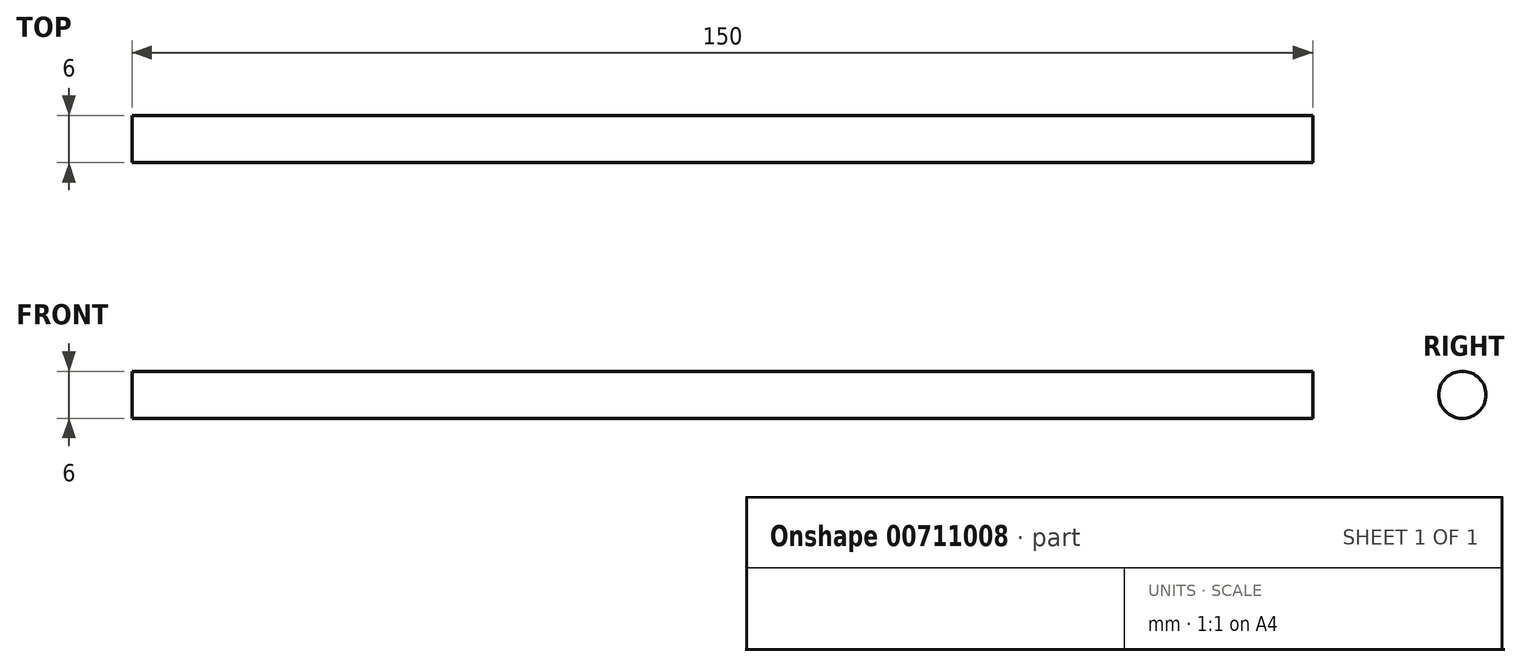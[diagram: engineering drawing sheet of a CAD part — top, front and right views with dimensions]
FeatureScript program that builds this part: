
annotation { "Feature Type Name" : "Feature", "Feature Type Description" : "" }
export const myFeature = defineFeature(function(context is Context, id is Id, definition is map)
    precondition{}
    {
        {
            var Q0;
            Q0=qCreatedBy(makeId("Right.planeOp"),FACE);
            var sketch = newSketch(context, id + "F0", { "sketchPlane" : qUnion([Q0])});
            skCircle(sketch, "E0", {"center": v(0, 0) * mm, "radius": 3 * mm});
            skSolve(sketch);
        }
        {
            var Q0;
            Q0 = qSketchRegion(id + "F0", true);
            extrude(context, id + "F1", {"entities" : qUnion([Q0]), "depth" : 150 * mm, "offsetDistance" : 25 * mm});
        }
    });
